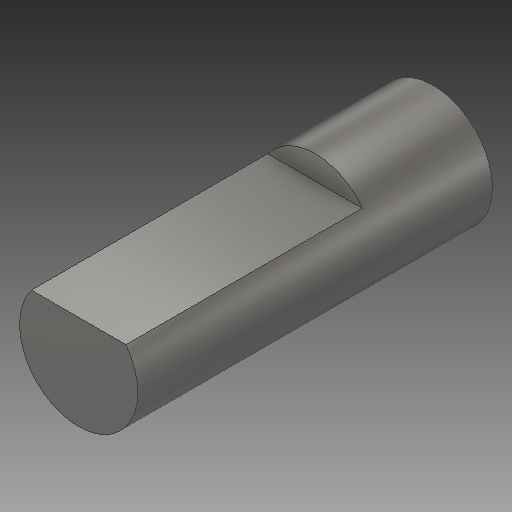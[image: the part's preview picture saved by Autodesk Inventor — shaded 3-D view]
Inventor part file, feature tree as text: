
AUTODESK INVENTOR PART (.ipt)
format: ipt  version: 2018 (Build 220112000, 112)  size: 116,224 bytes
history: native  units: mm
features: extrude x2, sketch x2, plane x1, projected_geometry x1
ambient origin geometry x8: Origin, YZ Plane, XZ Plane, XY Plane, X Axis, Y Axis, Z Axis, Center Point
bodies: Solid1 (feature_tree)
feature tree (6):
  extrude  "Extrusion1"  Depth=15.0mm TaperAngle=0.0deg
  plane  "Work Plane2"
  extrude  "Extrusion2"  Depth=10.0mm
  sketch  "Sketch1"  dims[d0=5.0mm d1=15.0mm d2=0.0mm]
  sketch  "Sketch2"  dims[d5=1.0mm d6=10.0mm d7=15.0mm d8=0.0mm]
  projected_geometry  "Projected Loop1"
